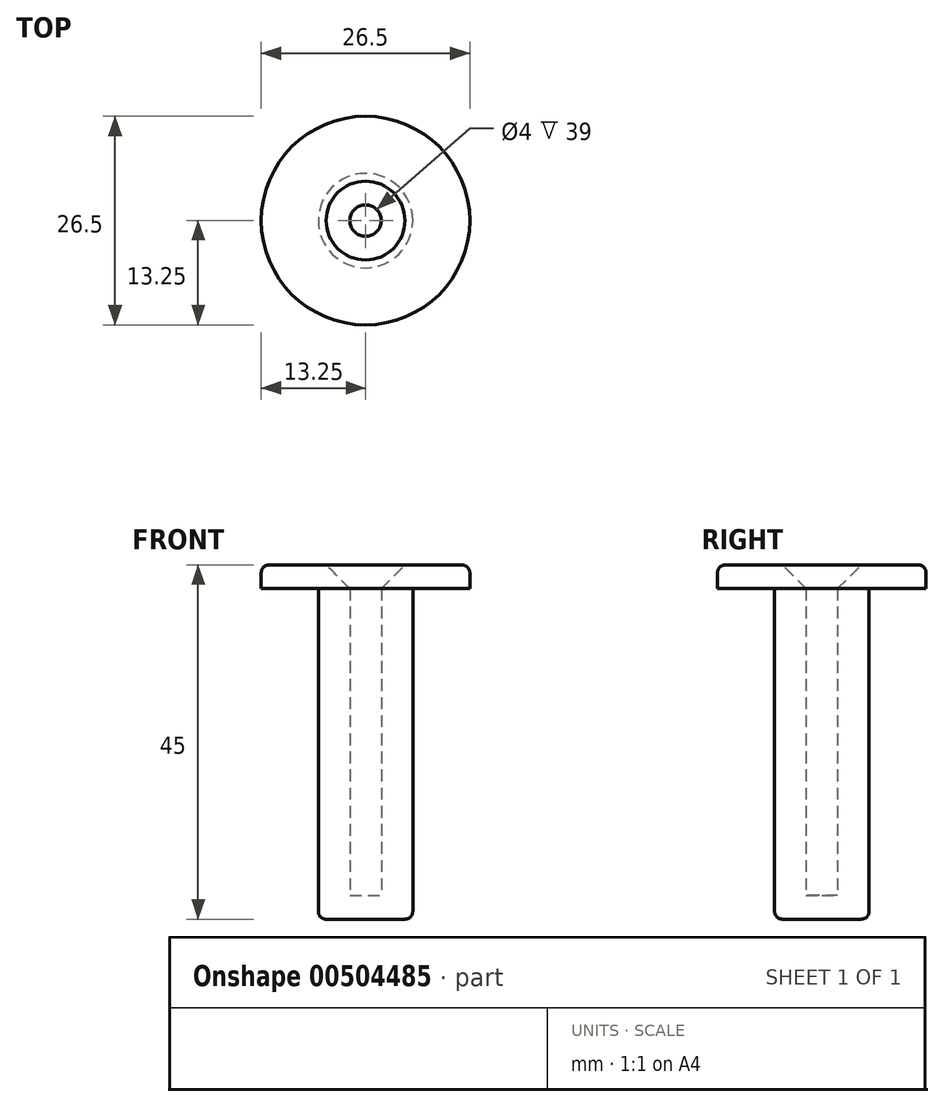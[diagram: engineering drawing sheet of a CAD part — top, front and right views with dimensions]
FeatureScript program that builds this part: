
annotation { "Feature Type Name" : "Feature", "Feature Type Description" : "" }
export const myFeature = defineFeature(function(context is Context, id is Id, definition is map)
    precondition{}
    {
        {
            var Q0;
            Q0=qCreatedBy(makeId("Front.planeOp"),FACE);
            var sketch = newSketch(context, id + "F0", { "sketchPlane" : qUnion([Q0])});
            skLineSegment(sketch, "E0", {"start": v(0, 0) * mm, "end": v(-6, 0) * mm});
            skLineSegment(sketch, "E1", {"start": v(-6, 0) * mm, "end": v(-6, 42) * mm});
            skLineSegment(sketch, "E2", {"start": v(-6, 42) * mm, "end": v(-13.25, 42) * mm});
            skLineSegment(sketch, "E3", {"start": v(-13.25, 42) * mm, "end": v(-13.25, 45) * mm});
            skLineSegment(sketch, "E4", {"start": v(-13.25, 45) * mm, "end": v(-5, 45) * mm});
            skLineSegment(sketch, "E5", {"start": v(-2, 42) * mm, "end": v(-2, 3) * mm});
            skLineSegment(sketch, "E6", {"start": v(-2, 3) * mm, "end": v(0, 3) * mm});
            skLineSegment(sketch, "E7", {"start": v(-5, 45) * mm, "end": v(-2, 42) * mm});
            skPoint(sketch, "E8.orphan", {"position": v(-2, 45) * mm});
            skLineSegment(sketch, "E9", {"start": v(0, 0) * mm, "end": v(0, 3) * mm});
            skSolve(sketch);
        }
        {
            var Q0;
            Q0=makeQuery(id+"F0.imprint","IMPRINT",FACE,{"disambiguationData":[TD([[makeQuery(id+"F0.imprint","IMPRINT",EDGE,{"derivedFrom":sQuery(id+"F0.wireOp",EDGE,"E0")}),-1.0]])]});
            var Q1;
            Q1 = qSketchRegion(id + "F0", true);
            var Q2;
            Q2=sQuery(id+"F0.wireOp",EDGE,"E9");
            revolve(context, id + "F1", {"entities" : qUnion([Q0, Q1]), "axis" : qUnion([Q2]), "revolveType" : RevolveType.FULL});
        }
        {
            var Q0;
            Q0=makeQuery(id+"F1.opRevolve","SWEPT_EDGE",EDGE,{"disambiguationData":[OSD([sQuery(id+"F0.wireOp",EDGE,"E0"),sQuery(id+"F0.wireOp",EDGE,"E1")])]});
            var Q1;
            Q1=makeQuery(id+"F1.opRevolve","SWEPT_EDGE",EDGE,{"disambiguationData":[OSD([sQuery(id+"F0.wireOp",EDGE,"E3"),sQuery(id+"F0.wireOp",EDGE,"E4")])]});
            fillet(context, id + "F2", {"entities" : qUnion([Q0, Q1]), "radius" : 1 * mm, "tangentPropagation" : true, "allowEdgeOverflow" : false});
        }
    });
